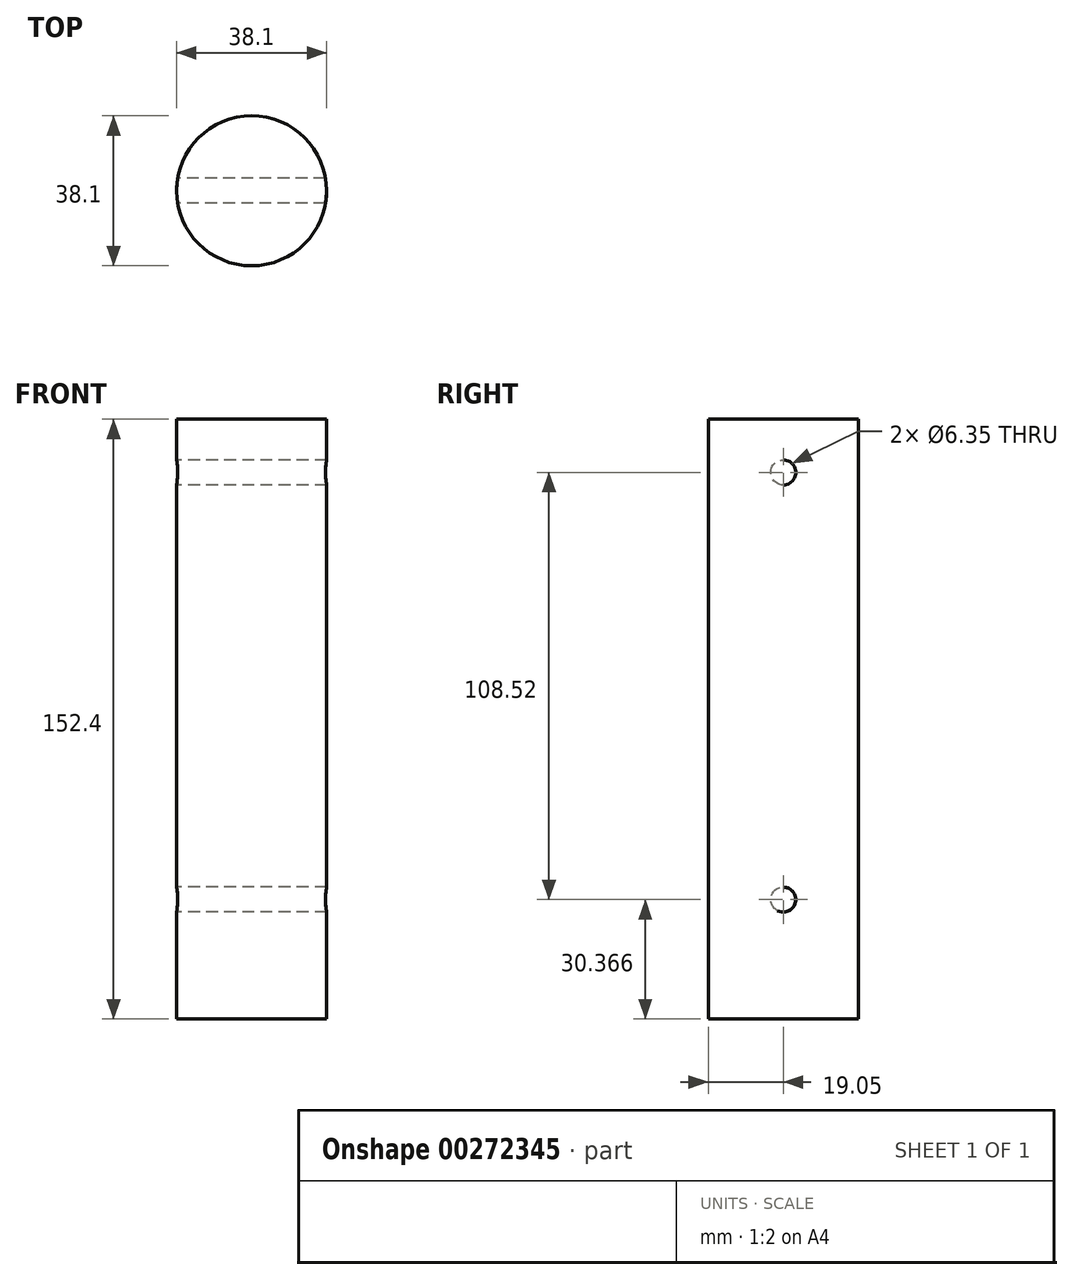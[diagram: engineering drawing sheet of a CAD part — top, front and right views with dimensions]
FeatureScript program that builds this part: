
annotation { "Feature Type Name" : "Feature", "Feature Type Description" : "" }
export const myFeature = defineFeature(function(context is Context, id is Id, definition is map)
    precondition{}
    {
        {
            var Q0;
            Q0=qCreatedBy(makeId("Top.planeOp"),FACE);
            var sketch = newSketch(context, id + "F0", { "sketchPlane" : qUnion([Q0])});
            skCircle(sketch, "E0", {"center": v(0, 0) * mm, "radius": 19.05 * mm});
            skSolve(sketch);
        }
        {
            var Q0;
            Q0 = qSketchRegion(id + "F0", true);
            extrude(context, id + "F1", {"entities" : qUnion([Q0]), "endBound" : BoundingType.SYMMETRIC, "depth" : 152.4 * mm});
        }
        {
            var Q0;
            Q0=qCreatedBy(makeId("Right.planeOp"),FACE);
            var sketch = newSketch(context, id + "F2", { "sketchPlane" : qUnion([Q0])});
            skCircle(sketch, "E1", {"center": v(0, 62.69) * mm, "radius": 3.18 * mm});
            skCircle(sketch, "E2", {"center": v(0, -45.83) * mm, "radius": 3.18 * mm});
            skSolve(sketch);
        }
        {
            var Q0;
            Q0 = qSketchRegion(id + "F2", true);
            extrude(context, id + "F3", {"entities" : qUnion([Q0]), "operationType" : NewBodyOperationType.REMOVE, "endBound" : BoundingType.SYMMETRIC, "depth" : 76.2 * mm});
        }
    });
